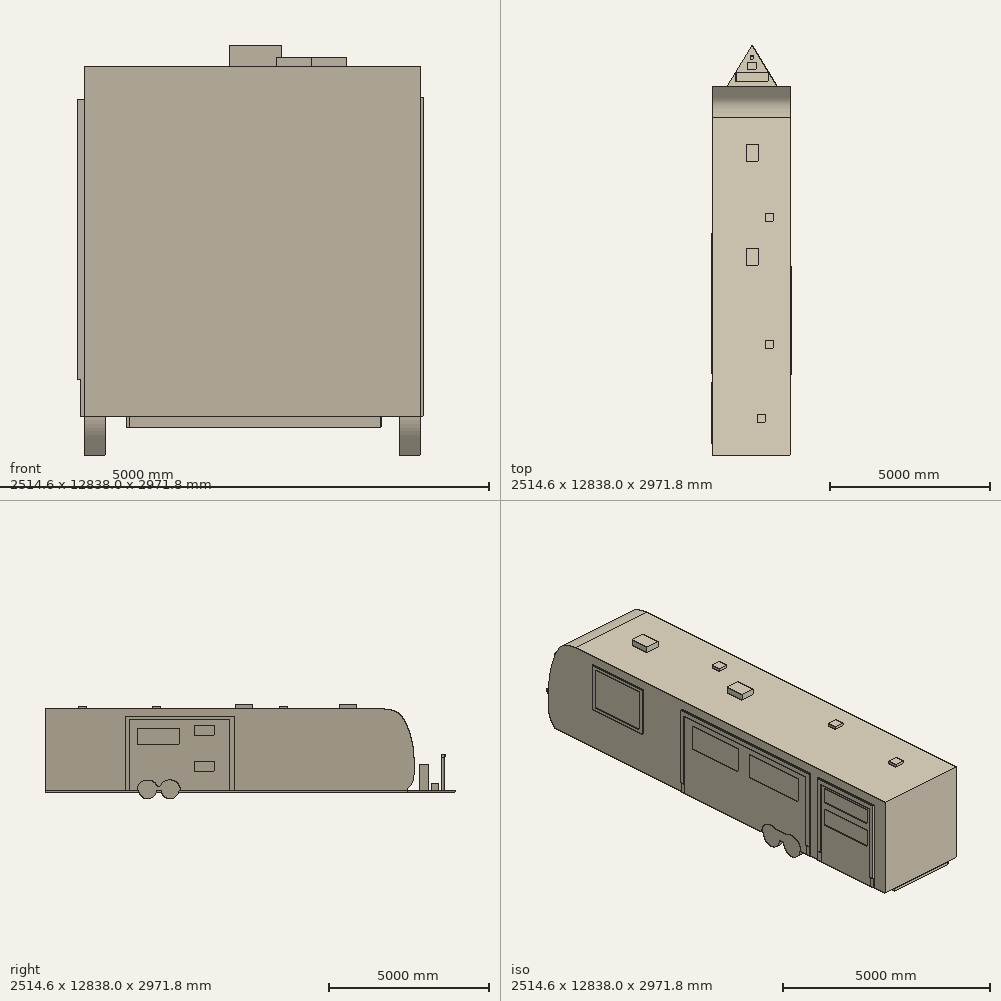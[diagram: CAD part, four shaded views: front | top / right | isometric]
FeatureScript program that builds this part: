
annotation { "Feature Type Name" : "Feature", "Feature Type Description" : "" }
export const myFeature = defineFeature(function(context is Context, id is Id, definition is map)
    precondition{}
    {
        {
            var Q0;
            Q0=qCreatedBy(makeId("Right.planeOp"),FACE);
            var sketch = newSketch(context, id + "F0", { "sketchPlane" : qUnion([Q0])});
            skLineSegment(sketch, "E0.bottom", {"start": v(-92.94, 2504.2) * mm, "end": v(11489.46, 2504.2) * mm});
            skLineSegment(sketch, "E0.top", {"start": v(-92.94, -35.8) * mm, "end": v(11489.46, -35.8) * mm});
            skLineSegment(sketch, "E0.left", {"start": v(-92.94, 2504.2) * mm, "end": v(-92.94, -35.8) * mm});
            skLineSegment(sketch, "E0.right", {"start": v(11489.46, 2504.2) * mm, "end": v(11489.46, -35.8) * mm});
            skSolve(sketch);
        }
        {
            var Q0;
            Q0 = qSketchRegion(id + "F0", true);
            extrude(context, id + "F1", {"entities" : qUnion([Q0]), "depth" : 2438.4 * mm});
        }
        {
            var Q0;
            Q0=makeQuery(id+"F1.opExtrude","CAP_FACE",FACE,{"disambiguationData":[OSD([sQuery(id+"F0.wireOp",EDGE,"E0.bottom"),sQuery(id+"F0.wireOp",EDGE,"E0.top"),sQuery(id+"F0.wireOp",EDGE,"E0.left"),sQuery(id+"F0.wireOp",EDGE,"E0.right")])],"isStart":false});
            var sketch = newSketch(context, id + "F2", { "sketchPlane" : qUnion([Q0])});
            skFitSpline(sketch, "E1", {"points": [v(11227.22, -35.8) * mm, v(11399.13, 196.48) * mm, v(11452.15, 611.33) * mm, v(11421.45, 1291.05) * mm, v(11256.96, 1907.06) * mm, v(10951.77, 2379.6) * mm, v(10498.91, 2504.2) * mm], "startDerivative": vector(1581.34, 1665.5) * mm, "endDerivative": vector(-3034.29, 317.5) * mm});
            skSolve(sketch);
        }
        {
            var Q0;
            Q0 = qSketchRegion(id + "F2", true);
            var Q1;
            {var subQ0=sQuery(id+"F2.wireOp",EDGE,"E1");Q1=makeQuery(id+"F2.imprint","IMPRINT",FACE,{"disambiguationData":[TD([[makeQuery(id+"F2.imprint","IMPRINT",EDGE,{"derivedFrom":subQ0}),-1.0]])]});}
            extrude(context, id + "F3", {"entities" : qUnion([Q0, Q1]), "operationType" : NewBodyOperationType.REMOVE, "endBound" : BoundingType.THROUGH_ALL, "oppositeDirection" : true, "depth" : 25.4 * mm});
        }
        {
            var Q0;
            Q0=makeQuery(id+"F1.opExtrude","CAP_FACE",FACE,{"disambiguationData":[OSD([sQuery(id+"F0.wireOp",EDGE,"E0.bottom"),sQuery(id+"F0.wireOp",EDGE,"E0.top"),sQuery(id+"F0.wireOp",EDGE,"E0.left"),sQuery(id+"F0.wireOp",EDGE,"E0.right")])],"isStart":true});
            var sketch = newSketch(context, id + "F4", { "sketchPlane" : qUnion([Q0])});
            skLineSegment(sketch, "E2", {"start": v(-11413.21, 234.93) * mm, "end": v(-3972.23, 234.93) * mm});
            skLineSegment(sketch, "E3.bottom", {"start": v(-294.2, 2264.02) * mm, "end": v(-2196.7, 2264.02) * mm});
            skLineSegment(sketch, "E3.top", {"start": v(-294.2, -35.8) * mm, "end": v(-2196.7, -35.8) * mm});
            skLineSegment(sketch, "E3.left", {"start": v(-294.2, 2264.02) * mm, "end": v(-294.2, -35.8) * mm});
            skLineSegment(sketch, "E3.right", {"start": v(-2196.7, 2264.02) * mm, "end": v(-2196.7, -35.8) * mm});
            skLineSegment(sketch, "E4.bottom", {"start": v(-2467, 2264.02) * mm, "end": v(-6864.6, 2264.02) * mm});
            skLineSegment(sketch, "E4.top", {"start": v(-2467, -35.8) * mm, "end": v(-6864.6, -35.8) * mm});
            skLineSegment(sketch, "E4.left", {"start": v(-2467, 2264.02) * mm, "end": v(-2467, -35.8) * mm});
            skLineSegment(sketch, "E4.right", {"start": v(-6864.6, 2264.02) * mm, "end": v(-6864.6, -35.8) * mm});
            skPoint(sketch, "E5.endSnap0", {"position": v(-4665.8, 2264.02) * mm});
            skLineSegment(sketch, "E6.bottom", {"start": v(-8189.46, 2264.02) * mm, "end": v(-9928.19, 2264.02) * mm});
            skLineSegment(sketch, "E6.top", {"start": v(-8189.46, 1028.62) * mm, "end": v(-9928.19, 1028.62) * mm});
            skLineSegment(sketch, "E6.left", {"start": v(-8189.46, 2264.02) * mm, "end": v(-8189.46, 1028.62) * mm});
            skLineSegment(sketch, "E6.right", {"start": v(-9928.19, 2264.02) * mm, "end": v(-9928.19, 1028.62) * mm});
            skLineSegment(sketch, "E7.bottom", {"start": v(-9823.16, 2172.22) * mm, "end": v(-8306.15, 2172.22) * mm});
            skLineSegment(sketch, "E7.top", {"start": v(-9823.16, 1121.98) * mm, "end": v(-8306.15, 1121.98) * mm});
            skLineSegment(sketch, "E7.left", {"start": v(-9823.16, 2172.22) * mm, "end": v(-9823.16, 1121.98) * mm});
            skLineSegment(sketch, "E7.right", {"start": v(-8306.15, 2172.22) * mm, "end": v(-8306.15, 1121.98) * mm});
            skLineSegment(sketch, "E8.bottom", {"start": v(-6765.8, 2148.88) * mm, "end": v(-5554.68, 2148.88) * mm});
            skLineSegment(sketch, "E8.left", {"start": v(-6765.8, 2148.88) * mm, "end": v(-6765.8, 234.93) * mm});
            skLineSegment(sketch, "E8.right", {"start": v(-2582.35, 2148.88) * mm, "end": v(-2582.35, 234.93) * mm});
            skLineSegment(sketch, "E9", {"start": v(-5554.68, 2148.88) * mm, "end": v(-2582.35, 2148.88) * mm});
            skLineSegment(sketch, "E10.bottom", {"start": v(-2075.31, 2148.88) * mm, "end": v(-405.84, 2148.88) * mm});
            skLineSegment(sketch, "E10.left", {"start": v(-2075.31, 2148.88) * mm, "end": v(-2075.31, 234.93) * mm});
            skLineSegment(sketch, "E10.right", {"start": v(-405.84, 2148.88) * mm, "end": v(-405.84, 234.93) * mm});
            skLineSegment(sketch, "E11.bottom", {"start": v(-6515.67, 1954) * mm, "end": v(-4923.13, 1954) * mm});
            skLineSegment(sketch, "E11.top", {"start": v(-6515.67, 1310.39) * mm, "end": v(-4923.13, 1310.39) * mm});
            skLineSegment(sketch, "E11.left", {"start": v(-6515.67, 1954) * mm, "end": v(-6515.67, 1310.39) * mm});
            skLineSegment(sketch, "E11.right", {"start": v(-4923.13, 1954) * mm, "end": v(-4923.13, 1310.39) * mm});
            skLineSegment(sketch, "E12.bottom", {"start": v(-4560.07, 1954) * mm, "end": v(-2860.27, 1954) * mm});
            skLineSegment(sketch, "E12.top", {"start": v(-4560.07, 1310.39) * mm, "end": v(-2860.27, 1310.39) * mm});
            skLineSegment(sketch, "E12.left", {"start": v(-4560.07, 1954) * mm, "end": v(-4560.07, 1310.39) * mm});
            skLineSegment(sketch, "E12.right", {"start": v(-2860.27, 1954) * mm, "end": v(-2860.27, 1310.39) * mm});
            skPoint(sketch, "E13.orphan", {"position": v(451.54, 2264.02) * mm});
            skLineSegment(sketch, "E14.bottom", {"start": v(-1987.57, 2047.8) * mm, "end": v(-505.56, 2047.8) * mm});
            skLineSegment(sketch, "E14.top", {"start": v(-1987.57, 1662.7) * mm, "end": v(-505.56, 1662.7) * mm});
            skLineSegment(sketch, "E14.left", {"start": v(-1987.57, 2047.8) * mm, "end": v(-1987.57, 1662.7) * mm});
            skLineSegment(sketch, "E14.right", {"start": v(-505.56, 2047.8) * mm, "end": v(-505.56, 1662.7) * mm});
            skLineSegment(sketch, "E15.bottom", {"start": v(-1975.9, 1487.66) * mm, "end": v(-517.23, 1487.66) * mm});
            skLineSegment(sketch, "E15.top", {"start": v(-1975.9, 1032.56) * mm, "end": v(-517.23, 1032.56) * mm});
            skLineSegment(sketch, "E15.left", {"start": v(-1975.9, 1487.66) * mm, "end": v(-1975.9, 1032.56) * mm});
            skLineSegment(sketch, "E15.right", {"start": v(-517.23, 1487.66) * mm, "end": v(-517.23, 1032.56) * mm});
            skCircle(sketch, "E16", {"center": v(-3107.83, -35.8) * mm, "radius": 279.4 * mm});
            skCircle(sketch, "E17", {"center": v(-3807.99, -35.8) * mm, "radius": 279.4 * mm});
            skArc(sketch, "E18", {"start": v(-3542.35, 130.2) * mm, "mid": v(-3897.19, 267.2) * mm, "end": v(-4127.14, -35.8) * mm});
            skArc(sketch, "E19", {"start": v(-2783.43, -35.8) * mm, "mid": v(-3019.85, 266.52) * mm, "end": v(-3378.61, 130.2) * mm});
            skArc(sketch, "E20", {"start": v(-3542.35, 130.2) * mm, "mid": v(-3460.48, 80.08) * mm, "end": v(-3378.61, 130.2) * mm});
            skLineSegment(sketch, "E21.trimOffspring", {"start": v(-3649.39, 234.93) * mm, "end": v(-3268.73, 234.93) * mm});
            skLineSegment(sketch, "E22.trimOffspring", {"start": v(-2944.75, 234.93) * mm, "end": v(92.94, 234.93) * mm});
            skLineSegment(sketch, "E23", {"start": v(-6765.8, 234.93) * mm, "end": v(-6765.8, -35.8) * mm});
            skLineSegment(sketch, "E24", {"start": v(-2582.35, 234.93) * mm, "end": v(-2582.35, -35.8) * mm});
            skLineSegment(sketch, "E25", {"start": v(-2075.31, 234.93) * mm, "end": v(-2075.31, -35.8) * mm});
            skLineSegment(sketch, "E26", {"start": v(-405.84, 234.93) * mm, "end": v(-405.84, -35.8) * mm});
            skSolve(sketch);
        }
        {
            var Q0;
            Q0=makeQuery(id+"F4.imprint","IMPRINT",FACE,{"disambiguationData":[TD([[makeQuery(id+"F4.imprint","IMPRINT",EDGE,{"derivedFrom":sQuery(id+"F4.wireOp",EDGE,"E6.top")}),-1.0]])]});
            var Q1;
            Q1=makeQuery(id+"F4.imprint","IMPRINT",FACE,{"disambiguationData":[TD([[makeQuery(id+"F4.imprint","IMPRINT",EDGE,{"derivedFrom":sQuery(id+"F4.wireOp",EDGE,"E8.bottom")}),1.0]])]});
            var Q2;
            {var subQ1=sQuery(id+"F4.wireOp",EDGE,"E3.bottom");Q2=makeQuery(id+"F4.imprint","IMPRINT",FACE,{"disambiguationData":[TD([[makeQuery(id+"F4.imprint","IMPRINT",EDGE,{"derivedFrom":subQ1}),1.0]])]});}
            extrude(context, id + "F5", {"entities" : qUnion([Q0, Q1, Q2]), "operationType" : NewBodyOperationType.ADD, "depth" : 25.4 * mm});
        }
        {
            var Q0;
            {var subQ0=sQuery(id+"F4.wireOp",EDGE,"E23");Q0=makeQuery(id+"F4.imprint","IMPRINT",FACE,{"disambiguationData":[TD([[makeQuery(id+"F4.imprint","IMPRINT",EDGE,{"derivedFrom":subQ0}),-1.0]])]});}
            var Q1;
            {var subQ3=sQuery(id+"F4.wireOp",EDGE,"E24");Q1=makeQuery(id+"F4.imprint","IMPRINT",FACE,{"disambiguationData":[TD([[makeQuery(id+"F4.imprint","IMPRINT",EDGE,{"derivedFrom":subQ3}),1.0]])]});}
            var Q2;
            {var subQ3=sQuery(id+"F4.wireOp",EDGE,"E25");Q2=makeQuery(id+"F4.imprint","IMPRINT",FACE,{"disambiguationData":[TD([[makeQuery(id+"F4.imprint","IMPRINT",EDGE,{"derivedFrom":subQ3}),-1.0]])]});}
            var Q3;
            {var subQ3=sQuery(id+"F4.wireOp",EDGE,"E26");Q3=makeQuery(id+"F4.imprint","IMPRINT",FACE,{"disambiguationData":[TD([[makeQuery(id+"F4.imprint","IMPRINT",EDGE,{"derivedFrom":subQ3}),1.0]])]});}
            var Q4;
            Q4=makeQuery(id+"F5.opExtrude","CAP_FACE",FACE,{"disambiguationData":[OSD([sQuery(id+"F4.wireOp",EDGE,"E2"),sQuery(id+"F4.wireOp",EDGE,"E4.left"),sQuery(id+"F4.wireOp",EDGE,"E4.right"),sQuery(id+"F4.wireOp",EDGE,"E8.bottom"),sQuery(id+"F4.wireOp",EDGE,"E8.left"),sQuery(id+"F4.wireOp",EDGE,"E8.right"),sQuery(id+"F4.wireOp",EDGE,"E9"),sQuery(id+"F4.wireOp",EDGE,"E4.bottom"),sQuery(id+"F4.wireOp",EDGE,"E22.trimOffspring")])],"isStart":false});
            var Q5;
            Q5=makeQuery(id+"F5.opExtrude","CAP_FACE",FACE,{"disambiguationData":[OSD([sQuery(id+"F4.wireOp",EDGE,"E3.left"),sQuery(id+"F4.wireOp",EDGE,"E3.right"),sQuery(id+"F4.wireOp",EDGE,"E3.bottom"),sQuery(id+"F4.wireOp",EDGE,"E10.left"),sQuery(id+"F4.wireOp",EDGE,"E10.right"),sQuery(id+"F4.wireOp",EDGE,"E10.bottom"),sQuery(id+"F4.wireOp",EDGE,"E22.trimOffspring")])],"isStart":false});
            extrude(context, id + "F6", {"entities" : qUnion([Q0, Q1, Q2, Q3, Q4, Q5]), "operationType" : NewBodyOperationType.ADD, "depth" : 25.4 * mm});
        }
        {
            var Q0;
            Q0=makeQuery(id+"F4.imprint","IMPRINT",FACE,{"disambiguationData":[TD([[makeQuery(id+"F4.imprint","IMPRINT",EDGE,{"derivedFrom":sQuery(id+"F4.wireOp",EDGE,"E8.bottom")}),-1.0]])]});
            var Q1;
            {var subQ3=sQuery(id+"F4.wireOp",EDGE,"E23");Q1=makeQuery(id+"F4.imprint","IMPRINT",FACE,{"disambiguationData":[TD([[makeQuery(id+"F4.imprint","IMPRINT",EDGE,{"derivedFrom":subQ3}),1.0]])]});}
            var Q2;
            {var subQ3=sQuery(id+"F4.wireOp",EDGE,"E24");Q2=makeQuery(id+"F4.imprint","IMPRINT",FACE,{"disambiguationData":[TD([[makeQuery(id+"F4.imprint","IMPRINT",EDGE,{"derivedFrom":subQ3}),-1.0]])]});}
            var Q3;
            {var subQ0=sQuery(id+"F4.wireOp",EDGE,"E25");Q3=makeQuery(id+"F4.imprint","IMPRINT",FACE,{"disambiguationData":[TD([[makeQuery(id+"F4.imprint","IMPRINT",EDGE,{"derivedFrom":subQ0}),1.0]])]});}
            var Q4;
            {var subQ1=sQuery(id+"F4.wireOp",EDGE,"E10.left");Q4=makeQuery(id+"F4.imprint","IMPRINT",FACE,{"disambiguationData":[TD([[makeQuery(id+"F4.imprint","IMPRINT",EDGE,{"derivedFrom":subQ1}),1.0]])]});}
            var Q5;
            Q5=makeQuery(id+"F4.imprint","IMPRINT",FACE,{"disambiguationData":[TD([[makeQuery(id+"F4.imprint","IMPRINT",EDGE,{"derivedFrom":sQuery(id+"F4.wireOp",EDGE,"E7.bottom")}),-1.0]])]});
            extrude(context, id + "F7", {"entities" : qUnion([Q0, Q1, Q2, Q3, Q4, Q5]), "operationType" : NewBodyOperationType.ADD, "depth" : 12.7 * mm});
        }
        {
            var Q0;
            Q0=makeQuery(id+"F7.opExtrude","CAP_EDGE",EDGE,{"disambiguationData":[OSD([sQuery(id+"F4.wireOp",EDGE,"E14.left")])],"isStart":false});
            var Q1;
            Q1=makeQuery(id+"F7.opExtrude","CAP_EDGE",EDGE,{"disambiguationData":[OSD([sQuery(id+"F4.wireOp",EDGE,"E14.bottom")])],"isStart":false});
            fillet(context, id + "F8", {"entities" : qUnion([Q0, Q1]), "radius" : 5.08 * mm, "tangentPropagation" : true, "allowEdgeOverflow" : false});
        }
        {
            var Q0;
            {var subQ0=sQuery(id+"F4.wireOp",EDGE,"E17");var subQ1=sQuery(id+"F4.wireOp",EDGE,"E4.top");var subQ2=makeQuery(id+"F4.imprint","INTERSECT",VERTEX,{"disambiguationData":[OD(0.0)],"derivedFrom":[subQ1,subQ0]});Q0=makeQuery(id+"F4.imprint","IMPRINT",FACE,{"disambiguationData":[TD([[makeQuery(id+"F4.imprint","IMPRINT",EDGE,{"disambiguationData":[TD([[subQ2,-1.0]])],"derivedFrom":subQ1}),-1.0]])]});}
            var Q1;
            {var subQ0=sQuery(id+"F4.wireOp",EDGE,"E17");var subQ1=sQuery(id+"F4.wireOp",EDGE,"E4.top");var subQ2=makeQuery(id+"F4.imprint","INTERSECT",VERTEX,{"disambiguationData":[OD(0.0)],"derivedFrom":[subQ1,subQ0]});Q1=makeQuery(id+"F4.imprint","IMPRINT",FACE,{"disambiguationData":[TD([[makeQuery(id+"F4.imprint","IMPRINT",EDGE,{"disambiguationData":[TD([[subQ2,-1.0]])],"derivedFrom":subQ1}),1.0]])]});}
            var Q2;
            {var subQ0=sQuery(id+"F4.wireOp",EDGE,"E16");var subQ1=sQuery(id+"F4.wireOp",EDGE,"E4.top");var subQ2=makeQuery(id+"F4.imprint","INTERSECT",VERTEX,{"disambiguationData":[OD(0.0)],"derivedFrom":[subQ1,subQ0]});Q2=makeQuery(id+"F4.imprint","IMPRINT",FACE,{"disambiguationData":[TD([[makeQuery(id+"F4.imprint","IMPRINT",EDGE,{"disambiguationData":[TD([[subQ2,-1.0]])],"derivedFrom":subQ1}),1.0]])]});}
            var Q3;
            {var subQ0=sQuery(id+"F4.wireOp",EDGE,"E16");var subQ1=sQuery(id+"F4.wireOp",EDGE,"E4.top");var subQ2=makeQuery(id+"F4.imprint","INTERSECT",VERTEX,{"disambiguationData":[OD(0.0)],"derivedFrom":[subQ1,subQ0]});Q3=makeQuery(id+"F4.imprint","IMPRINT",FACE,{"disambiguationData":[TD([[makeQuery(id+"F4.imprint","IMPRINT",EDGE,{"disambiguationData":[TD([[subQ2,-1.0]])],"derivedFrom":subQ1}),-1.0]])]});}
            extrude(context, id + "F9", {"entities" : qUnion([Q0, Q1, Q2, Q3]), "operationType" : NewBodyOperationType.ADD, "oppositeDirection" : true, "depth" : 152.4 * mm});
        }
        {
            var Q0;
            Q0=makeQuery(id+"F1.opExtrude","CAP_FACE",FACE,{"disambiguationData":[OSD([sQuery(id+"F0.wireOp",EDGE,"E0.bottom"),sQuery(id+"F0.wireOp",EDGE,"E0.top"),sQuery(id+"F0.wireOp",EDGE,"E0.left"),sQuery(id+"F0.wireOp",EDGE,"E0.right")])],"isStart":false});
            var sketch = newSketch(context, id + "F10", { "sketchPlane" : qUnion([Q0])});
            skCircle(sketch, "E27", {"center": v(3106.1, -35.8) * mm, "radius": 279.4 * mm});
            skCircle(sketch, "E28", {"center": v(3810.96, -35.8) * mm, "radius": 279.4 * mm});
            skArc(sketch, "E29", {"start": v(3378.7, 135.27) * mm, "mid": v(3015.5, 266.37) * mm, "end": v(2775.1, -35.8) * mm});
            skArc(sketch, "E30", {"start": v(4130.28, -35.8) * mm, "mid": v(3897.32, 267.74) * mm, "end": v(3538.36, 135.27) * mm});
            skArc(sketch, "E31", {"start": v(3378.7, 135.27) * mm, "mid": v(3398.12, 103.41) * mm, "end": v(3429.4, 83.07) * mm});
            skLineSegment(sketch, "E32", {"start": v(11412.26, 231.97) * mm, "end": v(3977.8, 231.97) * mm});
            skLineSegment(sketch, "E33.trimOffspring", {"start": v(2935.84, 231.97) * mm, "end": v(-92.94, 231.97) * mm});
            skLineSegment(sketch, "E34.trimOffspring", {"start": v(3637.72, 231.97) * mm, "end": v(3275.74, 231.97) * mm});
            skLineSegment(sketch, "E35.bottom", {"start": v(2402.79, -35.8) * mm, "end": v(5820.45, -35.8) * mm});
            skLineSegment(sketch, "E35.top", {"start": v(2402.79, 2278.16) * mm, "end": v(5820.45, 2278.16) * mm});
            skLineSegment(sketch, "E35.left", {"start": v(2402.79, -35.8) * mm, "end": v(2402.79, 2278.16) * mm});
            skLineSegment(sketch, "E35.right", {"start": v(5820.45, -35.8) * mm, "end": v(5820.45, 2278.16) * mm});
            skLineSegment(sketch, "E36.bottom", {"start": v(2541.72, 2157.75) * mm, "end": v(5663, 2157.75) * mm});
            skLineSegment(sketch, "E36.left", {"start": v(2541.72, 2157.75) * mm, "end": v(2541.72, 83.07) * mm});
            skLineSegment(sketch, "E36.right", {"start": v(5663, 2157.75) * mm, "end": v(5663, 83.07) * mm});
            skLineSegment(sketch, "E37.trimOffspring", {"start": v(3429.4, 83.07) * mm, "end": v(3487.66, 83.07) * mm});
            skArc(sketch, "E38.trimOffspring", {"start": v(3487.66, 83.07) * mm, "mid": v(3518.94, 103.41) * mm, "end": v(3538.36, 135.27) * mm});
            skLineSegment(sketch, "E39", {"start": v(5663.45, -35.8) * mm, "end": v(5663, 83.07) * mm});
            skLineSegment(sketch, "E40", {"start": v(2534.2, -35.8) * mm, "end": v(2541.72, 83.07) * mm});
            skLineSegment(sketch, "E41.bottom", {"start": v(2778.91, 1890.63) * mm, "end": v(4088.83, 1890.63) * mm});
            skLineSegment(sketch, "E41.top", {"start": v(2778.91, 1402) * mm, "end": v(4088.83, 1402) * mm});
            skLineSegment(sketch, "E41.left", {"start": v(2778.91, 1890.63) * mm, "end": v(2778.91, 1402) * mm});
            skLineSegment(sketch, "E41.right", {"start": v(4088.83, 1890.63) * mm, "end": v(4088.83, 1402) * mm});
            skSolve(sketch);
        }
        {
            var Q0;
            {var subQ5=sQuery(id+"F10.wireOp",EDGE,"E39");Q0=makeQuery(id+"F10.imprint","IMPRINT",FACE,{"disambiguationData":[TD([[makeQuery(id+"F10.imprint","IMPRINT",EDGE,{"derivedFrom":subQ5}),-1.0]])]});}
            var Q1;
            {var subQ0=sQuery(id+"F10.wireOp",EDGE,"E40");Q1=makeQuery(id+"F10.imprint","IMPRINT",FACE,{"disambiguationData":[TD([[makeQuery(id+"F10.imprint","IMPRINT",EDGE,{"derivedFrom":subQ0}),1.0]])]});}
            var Q2;
            {var subQ1=sQuery(id+"F10.wireOp",EDGE,"E35.top");Q2=makeQuery(id+"F10.imprint","IMPRINT",FACE,{"disambiguationData":[TD([[makeQuery(id+"F10.imprint","IMPRINT",EDGE,{"derivedFrom":subQ1}),-1.0]])]});}
            extrude(context, id + "F11", {"entities" : qUnion([Q0, Q1, Q2]), "operationType" : NewBodyOperationType.ADD, "depth" : 25.4 * mm});
        }
        {
            var Q0;
            {var subQ4=sQuery(id+"F10.wireOp",EDGE,"E34.trimOffspring");Q0=makeQuery(id+"F10.imprint","IMPRINT",FACE,{"disambiguationData":[TD([[makeQuery(id+"F10.imprint","IMPRINT",EDGE,{"derivedFrom":subQ4}),-1.0]])]});}
            var Q1;
            {var subQ0=sQuery(id+"F10.wireOp",EDGE,"E40");Q1=makeQuery(id+"F10.imprint","IMPRINT",FACE,{"disambiguationData":[TD([[makeQuery(id+"F10.imprint","IMPRINT",EDGE,{"derivedFrom":subQ0}),-1.0]])]});}
            var Q2;
            {var subQ1=sQuery(id+"F10.wireOp",EDGE,"E31");Q2=makeQuery(id+"F10.imprint","IMPRINT",FACE,{"disambiguationData":[TD([[makeQuery(id+"F10.imprint","IMPRINT",EDGE,{"derivedFrom":subQ1}),1.0]])]});}
            var Q3;
            {var subQ0=sQuery(id+"F10.wireOp",EDGE,"E39");Q3=makeQuery(id+"F10.imprint","IMPRINT",FACE,{"disambiguationData":[TD([[makeQuery(id+"F10.imprint","IMPRINT",EDGE,{"derivedFrom":subQ0}),1.0]])]});}
            extrude(context, id + "F12", {"entities" : qUnion([Q0, Q1, Q2, Q3]), "operationType" : NewBodyOperationType.ADD, "depth" : 12.7 * mm});
        }
        {
            var Q0;
            {var subQ0=sQuery(id+"F10.wireOp",EDGE,"E35.bottom");var subQ1=sQuery(id+"F10.wireOp",EDGE,"E27");var subQ2=makeQuery(id+"F10.imprint","INTERSECT",VERTEX,{"disambiguationData":[OD(0.0)],"derivedFrom":[subQ1,subQ0]});Q0=makeQuery(id+"F10.imprint","IMPRINT",FACE,{"disambiguationData":[TD([[makeQuery(id+"F10.imprint","IMPRINT",EDGE,{"disambiguationData":[TD([[subQ2,1.0]])],"derivedFrom":subQ1}),1.0]])]});}
            var Q1;
            {var subQ0=sQuery(id+"F10.wireOp",EDGE,"E35.bottom");var subQ1=sQuery(id+"F10.wireOp",EDGE,"E27");var subQ2=makeQuery(id+"F10.imprint","INTERSECT",VERTEX,{"disambiguationData":[OD(0.0)],"derivedFrom":[subQ1,subQ0]});Q1=makeQuery(id+"F10.imprint","IMPRINT",FACE,{"disambiguationData":[TD([[makeQuery(id+"F10.imprint","IMPRINT",EDGE,{"disambiguationData":[TD([[subQ2,-1.0]])],"derivedFrom":subQ1}),1.0]])]});}
            var Q2;
            {var subQ0=sQuery(id+"F10.wireOp",EDGE,"E35.bottom");var subQ1=sQuery(id+"F10.wireOp",EDGE,"E28");var subQ2=makeQuery(id+"F10.imprint","INTERSECT",VERTEX,{"disambiguationData":[OD(0.0)],"derivedFrom":[subQ1,subQ0]});Q2=makeQuery(id+"F10.imprint","IMPRINT",FACE,{"disambiguationData":[TD([[makeQuery(id+"F10.imprint","IMPRINT",EDGE,{"disambiguationData":[TD([[subQ2,-1.0]])],"derivedFrom":subQ1}),1.0]])]});}
            var Q3;
            {var subQ0=sQuery(id+"F10.wireOp",EDGE,"E35.bottom");var subQ1=sQuery(id+"F10.wireOp",EDGE,"E28");var subQ2=makeQuery(id+"F10.imprint","INTERSECT",VERTEX,{"disambiguationData":[OD(0.0)],"derivedFrom":[subQ1,subQ0]});Q3=makeQuery(id+"F10.imprint","IMPRINT",FACE,{"disambiguationData":[TD([[makeQuery(id+"F10.imprint","IMPRINT",EDGE,{"disambiguationData":[TD([[subQ2,1.0]])],"derivedFrom":subQ1}),1.0]])]});}
            extrude(context, id + "F13", {"entities" : qUnion([Q0, Q1, Q2, Q3]), "operationType" : NewBodyOperationType.ADD, "oppositeDirection" : true, "depth" : 152.4 * mm});
        }
        {
            var Q0;
            {var subQ0=sQuery(id+"F10.wireOp",EDGE,"E35.bottom");var subQ1=makeQuery(id+"F10.imprint","INTERSECT",VERTEX,{"derivedFrom":[subQ0,sQuery(id+"F10.wireOp",EDGE,"E39")]});var subQ2=makeQuery(id+"F10.imprint","INTERSECT",VERTEX,{"derivedFrom":[subQ0,sQuery(id+"F10.wireOp",EDGE,"E40")]});var subQ3=sQuery(id+"F0.wireOp",EDGE,"E0.top");var subQ5=sQuery(id+"F4.wireOp",EDGE,"E4.top");var subQ6=makeQuery(id+"F4.imprint","INTERSECT",VERTEX,{"derivedFrom":[subQ5,sQuery(id+"F4.wireOp",EDGE,"E23")]});var subQ7=makeQuery(id+"F4.imprint","INTERSECT",VERTEX,{"derivedFrom":[subQ5,sQuery(id+"F4.wireOp",EDGE,"E24")]});var subQ8=sQuery(id+"F4.wireOp",EDGE,"E3.top");Q0=makeQuery(id+"F12.boolean.opBoolean","MERGE",FACE,{"derivedFrom":[makeQuery(id+"F11.boolean.opBoolean","MERGE",FACE,{"derivedFrom":[makeQuery(id+"F7.boolean.opBoolean","MERGE",FACE,{"derivedFrom":[makeQuery(id+"F6.boolean.opBoolean","MERGE",FACE,{"derivedFrom":[makeQuery(id+"F1.opExtrude","SWEPT_FACE",FACE,{"disambiguationData":[OSD([subQ3])]}),makeQuery(id+"F6.opExtrude","SWEPT_FACE",FACE,{"disambiguationData":[OSD([subQ8]),TDD([makeQuery(id+"F4.imprint","IMPRINT",EDGE,{"disambiguationData":[TD([[makeQuery(id+"F4.imprint","INTERSECT",VERTEX,{"derivedFrom":[subQ8,sQuery(id+"F4.wireOp",EDGE,"E26")]}),1.0]])],"derivedFrom":subQ8})])]}),makeQuery(id+"F6.opExtrude","SWEPT_FACE",FACE,{"disambiguationData":[OSD([subQ8]),TDD([makeQuery(id+"F4.imprint","IMPRINT",EDGE,{"disambiguationData":[TD([[makeQuery(id+"F4.imprint","INTERSECT",VERTEX,{"derivedFrom":[subQ8,sQuery(id+"F4.wireOp",EDGE,"E25")]}),-1.0]])],"derivedFrom":subQ8})])]}),makeQuery(id+"F6.opExtrude","SWEPT_FACE",FACE,{"disambiguationData":[OSD([subQ5]),TDD([makeQuery(id+"F4.imprint","IMPRINT",EDGE,{"disambiguationData":[TD([[subQ7,1.0]])],"derivedFrom":subQ5})])]}),makeQuery(id+"F6.opExtrude","SWEPT_FACE",FACE,{"disambiguationData":[OSD([subQ5]),TDD([makeQuery(id+"F4.imprint","IMPRINT",EDGE,{"disambiguationData":[TD([[subQ6,-1.0]])],"derivedFrom":subQ5})])]})]}),makeQuery(id+"F7.opExtrude","SWEPT_FACE",FACE,{"disambiguationData":[OSD([subQ8])]}),makeQuery(id+"F7.opExtrude","SWEPT_FACE",FACE,{"disambiguationData":[OSD([subQ5]),TDD([makeQuery(id+"F4.imprint","IMPRINT",EDGE,{"disambiguationData":[TD([[makeQuery(id+"F4.imprint","INTERSECT",VERTEX,{"derivedFrom":[subQ5,sQuery(id+"F4.wireOp",EDGE,"E19")]}),1.0]])],"derivedFrom":subQ5})])]}),makeQuery(id+"F7.opExtrude","SWEPT_FACE",FACE,{"disambiguationData":[OSD([subQ5]),TDD([makeQuery(id+"F4.imprint","IMPRINT",EDGE,{"disambiguationData":[TD([[makeQuery(id+"F4.imprint","INTERSECT",VERTEX,{"derivedFrom":[subQ5,sQuery(id+"F4.wireOp",EDGE,"E18")]}),-1.0]])],"derivedFrom":subQ5})])]})]}),makeQuery(id+"F11.opExtrude","SWEPT_FACE",FACE,{"disambiguationData":[OSD([subQ0]),TDD([makeQuery(id+"F10.imprint","IMPRINT",EDGE,{"disambiguationData":[TD([[subQ2,1.0]])],"derivedFrom":subQ0})])]}),makeQuery(id+"F11.opExtrude","SWEPT_FACE",FACE,{"disambiguationData":[OSD([subQ0]),TDD([makeQuery(id+"F10.imprint","IMPRINT",EDGE,{"disambiguationData":[TD([[subQ1,-1.0]])],"derivedFrom":subQ0})])]})]}),makeQuery(id+"F12.opExtrude","SWEPT_FACE",FACE,{"disambiguationData":[OSD([subQ0]),TDD([makeQuery(id+"F10.imprint","IMPRINT",EDGE,{"disambiguationData":[TD([[makeQuery(id+"F10.imprint","INTERSECT",VERTEX,{"derivedFrom":[sQuery(id+"F10.wireOp",EDGE,"E29"),subQ0]}),1.0]])],"derivedFrom":subQ0})])]}),makeQuery(id+"F12.opExtrude","SWEPT_FACE",FACE,{"disambiguationData":[OSD([subQ0]),TDD([makeQuery(id+"F10.imprint","IMPRINT",EDGE,{"disambiguationData":[TD([[makeQuery(id+"F10.imprint","INTERSECT",VERTEX,{"derivedFrom":[sQuery(id+"F10.wireOp",EDGE,"E30"),subQ0]}),-1.0]])],"derivedFrom":subQ0})])]})]});}
            var sketch = newSketch(context, id + "F14", { "sketchPlane" : qUnion([Q0])});
            skLineSegment(sketch, "E42", {"start": v(304.51, -11227.22) * mm, "end": v(1230.43, -12745.1) * mm});
            skLineSegment(sketch, "E43", {"start": v(1230.43, -12745.1) * mm, "end": v(2156.35, -11227.22) * mm});
            skLineSegment(sketch, "E44", {"start": v(1219.2, -11227.22) * mm, "end": v(1230.43, -12318.8) * mm});
            skSolve(sketch);
        }
        {
            var Q0;
            {var subQ0=sQuery(id+"F14.wireOp",EDGE,"E42");Q0=makeQuery(id+"F14.imprint","IMPRINT",FACE,{"disambiguationData":[TD([[makeQuery(id+"F14.imprint","IMPRINT",EDGE,{"derivedFrom":subQ0}),1.0]])]});}
            var sketch = newSketch(context, id + "F15", { "sketchPlane" : qUnion([Q0])});
            skLineSegment(sketch, "E45", {"start": v(428.6, -11222.62) * mm, "end": v(1220.28, -12562.4) * mm});
            skLineSegment(sketch, "E46", {"start": v(1220.28, -12562.4) * mm, "end": v(2032.27, -11242.92) * mm});
            skSolve(sketch);
        }
        {
            var Q0;
            Q0=makeQuery(id+"F12.opExtrude","CAP_FACE",FACE,{"disambiguationData":[OSD([sQuery(id+"F10.wireOp",EDGE,"E29"),sQuery(id+"F10.wireOp",EDGE,"E30"),sQuery(id+"F10.wireOp",EDGE,"E31"),sQuery(id+"F10.wireOp",EDGE,"E35.bottom"),sQuery(id+"F10.wireOp",EDGE,"E36.bottom"),sQuery(id+"F10.wireOp",EDGE,"E36.left"),sQuery(id+"F10.wireOp",EDGE,"E36.right"),sQuery(id+"F10.wireOp",EDGE,"E37.trimOffspring"),sQuery(id+"F10.wireOp",EDGE,"E38.trimOffspring"),sQuery(id+"F10.wireOp",EDGE,"E39"),sQuery(id+"F10.wireOp",EDGE,"E40"),sQuery(id+"F10.wireOp",EDGE,"E41.bottom"),sQuery(id+"F10.wireOp",EDGE,"E41.top"),sQuery(id+"F10.wireOp",EDGE,"E41.left"),sQuery(id+"F10.wireOp",EDGE,"E41.right")])],"isStart":false});
            var sketch = newSketch(context, id + "F16", { "sketchPlane" : qUnion([Q0])});
            skLineSegment(sketch, "E47.bottom", {"start": v(4577.15, 1969.5) * mm, "end": v(5186.75, 1969.5) * mm});
            skLineSegment(sketch, "E47.top", {"start": v(4577.15, 1664.7) * mm, "end": v(5186.75, 1664.7) * mm});
            skLineSegment(sketch, "E47.left", {"start": v(4577.15, 1969.5) * mm, "end": v(4577.15, 1664.7) * mm});
            skLineSegment(sketch, "E47.right", {"start": v(5186.75, 1969.5) * mm, "end": v(5186.75, 1664.7) * mm});
            skLineSegment(sketch, "E48.bottom", {"start": v(4577.15, 858.86) * mm, "end": v(5186.75, 858.86) * mm});
            skLineSegment(sketch, "E48.top", {"start": v(4577.15, 554.06) * mm, "end": v(5186.75, 554.06) * mm});
            skLineSegment(sketch, "E48.left", {"start": v(4577.15, 858.86) * mm, "end": v(4577.15, 554.06) * mm});
            skLineSegment(sketch, "E48.right", {"start": v(5186.75, 858.86) * mm, "end": v(5186.75, 554.06) * mm});
            skSolve(sketch);
        }
        {
            var Q0;
            Q0=makeQuery(id+"F16.imprint","IMPRINT",FACE,{"disambiguationData":[TD([[makeQuery(id+"F16.imprint","IMPRINT",EDGE,{"derivedFrom":sQuery(id+"F16.wireOp",EDGE,"E47.bottom")}),-1.0]])]});
            var Q1;
            Q1=makeQuery(id+"F16.imprint","IMPRINT",FACE,{"disambiguationData":[TD([[makeQuery(id+"F16.imprint","IMPRINT",EDGE,{"derivedFrom":sQuery(id+"F16.wireOp",EDGE,"E48.bottom")}),-1.0]])]});
            extrude(context, id + "F17", {"entities" : qUnion([Q0, Q1]), "operationType" : NewBodyOperationType.ADD, "depth" : 6.35 * mm});
        }
        {
            var Q0;
            Q0=makeQuery(id+"F1.opExtrude","SWEPT_FACE",FACE,{"disambiguationData":[OSD([sQuery(id+"F0.wireOp",EDGE,"E0.bottom")])]});
            var sketch = newSketch(context, id + "F18", { "sketchPlane" : qUnion([Q0])});
            skLineSegment(sketch, "E49", {"start": v(1218.85, 11455.41) * mm, "end": v(1218.85, 8266.61) * mm, "construction": true});
            skLineSegment(sketch, "E50.bottom", {"start": v(1053.2, 9636) * mm, "end": v(1434.2, 9636) * mm});
            skLineSegment(sketch, "E50.top", {"start": v(1053.2, 9128) * mm, "end": v(1434.2, 9128) * mm});
            skLineSegment(sketch, "E50.left", {"start": v(1053.2, 9636) * mm, "end": v(1053.2, 9128) * mm});
            skLineSegment(sketch, "E50.right", {"start": v(1434.2, 9636) * mm, "end": v(1434.2, 9128) * mm});
            skSolve(sketch);
        }
        {
            var Q0;
            Q0 = qSketchRegion(id + "F18", true);
            extrude(context, id + "F19", {"entities" : qUnion([Q0]), "operationType" : NewBodyOperationType.ADD, "depth" : 152.4 * mm});
        }
        {
            var Q0;
            Q0=makeQuery(id+"F1.opExtrude","SWEPT_FACE",FACE,{"disambiguationData":[OSD([sQuery(id+"F0.wireOp",EDGE,"E0.bottom")])]});
            var sketch = newSketch(context, id + "F20", { "sketchPlane" : qUnion([Q0])});
            skLineSegment(sketch, "E51", {"start": v(1053.2, 6373.33) * mm, "end": v(1053.2, 5865.33) * mm});
            skLineSegment(sketch, "E52.bottom", {"start": v(1053.2, 6373.33) * mm, "end": v(1434.2, 6373.33) * mm});
            skLineSegment(sketch, "E52.top", {"start": v(1053.2, 5865.33) * mm, "end": v(1434.2, 5865.33) * mm});
            skLineSegment(sketch, "E52.right", {"start": v(1434.2, 6373.33) * mm, "end": v(1434.2, 5865.33) * mm});
            skSolve(sketch);
        }
        {
            var Q0;
            Q0 = qSketchRegion(id + "F20", true);
            extrude(context, id + "F21", {"entities" : qUnion([Q0]), "operationType" : NewBodyOperationType.ADD, "depth" : 152.4 * mm});
        }
        {
            var Q0;
            Q0=makeQuery(id+"F1.opExtrude","SWEPT_FACE",FACE,{"disambiguationData":[OSD([sQuery(id+"F0.wireOp",EDGE,"E0.bottom")])]});
            var sketch = newSketch(context, id + "F22", { "sketchPlane" : qUnion([Q0])});
            skLineSegment(sketch, "E53.bottom", {"start": v(1651.16, 7493.1) * mm, "end": v(1905.16, 7493.1) * mm});
            skLineSegment(sketch, "E53.top", {"start": v(1651.16, 7239.1) * mm, "end": v(1905.16, 7239.1) * mm});
            skLineSegment(sketch, "E53.left", {"start": v(1651.16, 7493.1) * mm, "end": v(1651.16, 7239.1) * mm});
            skLineSegment(sketch, "E53.right", {"start": v(1905.16, 7493.1) * mm, "end": v(1905.16, 7239.1) * mm});
            skLineSegment(sketch, "E54.bottom", {"start": v(1905.16, 3515.57) * mm, "end": v(1651.16, 3515.57) * mm});
            skLineSegment(sketch, "E54.top", {"start": v(1905.16, 3261.57) * mm, "end": v(1651.16, 3261.57) * mm});
            skLineSegment(sketch, "E54.left", {"start": v(1905.16, 3515.57) * mm, "end": v(1905.16, 3261.57) * mm});
            skLineSegment(sketch, "E54.right", {"start": v(1651.16, 3515.57) * mm, "end": v(1651.16, 3261.57) * mm});
            skLineSegment(sketch, "E55.bottom", {"start": v(1397.16, 932.38) * mm, "end": v(1651.16, 932.38) * mm});
            skLineSegment(sketch, "E55.top", {"start": v(1397.16, 1186.38) * mm, "end": v(1651.16, 1186.38) * mm});
            skLineSegment(sketch, "E55.left", {"start": v(1397.16, 932.38) * mm, "end": v(1397.16, 1186.38) * mm});
            skLineSegment(sketch, "E55.right", {"start": v(1651.16, 932.38) * mm, "end": v(1651.16, 1186.38) * mm});
            skSolve(sketch);
        }
        {
            var Q0;
            Q0 = qSketchRegion(id + "F22", true);
            extrude(context, id + "F23", {"entities" : qUnion([Q0]), "operationType" : NewBodyOperationType.ADD, "depth" : 63.5 * mm});
        }
        {
            var Q0;
            {var subQ0=sQuery(id+"F14.wireOp",EDGE,"E42");Q0=makeQuery(id+"F14.imprint","IMPRINT",FACE,{"disambiguationData":[TD([[makeQuery(id+"F14.imprint","IMPRINT",EDGE,{"derivedFrom":subQ0}),1.0]])]});}
            extrude(context, id + "F24", {"entities" : qUnion([Q0]), "depth" : 76.2 * mm});
        }
        {
            var Q0;
            {var subQ0=sQuery(id+"F10.wireOp",EDGE,"E35.bottom");var subQ1=makeQuery(id+"F10.imprint","INTERSECT",VERTEX,{"derivedFrom":[subQ0,sQuery(id+"F10.wireOp",EDGE,"E39")]});var subQ2=makeQuery(id+"F10.imprint","INTERSECT",VERTEX,{"derivedFrom":[subQ0,sQuery(id+"F10.wireOp",EDGE,"E40")]});var subQ3=sQuery(id+"F0.wireOp",EDGE,"E0.top");var subQ5=sQuery(id+"F4.wireOp",EDGE,"E4.top");var subQ6=makeQuery(id+"F4.imprint","INTERSECT",VERTEX,{"derivedFrom":[subQ5,sQuery(id+"F4.wireOp",EDGE,"E23")]});var subQ7=makeQuery(id+"F4.imprint","INTERSECT",VERTEX,{"derivedFrom":[subQ5,sQuery(id+"F4.wireOp",EDGE,"E24")]});var subQ8=sQuery(id+"F4.wireOp",EDGE,"E3.top");Q0=makeQuery(id+"F12.boolean.opBoolean","MERGE",FACE,{"derivedFrom":[makeQuery(id+"F11.boolean.opBoolean","MERGE",FACE,{"derivedFrom":[makeQuery(id+"F7.boolean.opBoolean","MERGE",FACE,{"derivedFrom":[makeQuery(id+"F6.boolean.opBoolean","MERGE",FACE,{"derivedFrom":[makeQuery(id+"F1.opExtrude","SWEPT_FACE",FACE,{"disambiguationData":[OSD([subQ3])]}),makeQuery(id+"F6.opExtrude","SWEPT_FACE",FACE,{"disambiguationData":[OSD([subQ8]),TDD([makeQuery(id+"F4.imprint","IMPRINT",EDGE,{"disambiguationData":[TD([[makeQuery(id+"F4.imprint","INTERSECT",VERTEX,{"derivedFrom":[subQ8,sQuery(id+"F4.wireOp",EDGE,"E26")]}),1.0]])],"derivedFrom":subQ8})])]}),makeQuery(id+"F6.opExtrude","SWEPT_FACE",FACE,{"disambiguationData":[OSD([subQ8]),TDD([makeQuery(id+"F4.imprint","IMPRINT",EDGE,{"disambiguationData":[TD([[makeQuery(id+"F4.imprint","INTERSECT",VERTEX,{"derivedFrom":[subQ8,sQuery(id+"F4.wireOp",EDGE,"E25")]}),-1.0]])],"derivedFrom":subQ8})])]}),makeQuery(id+"F6.opExtrude","SWEPT_FACE",FACE,{"disambiguationData":[OSD([subQ5]),TDD([makeQuery(id+"F4.imprint","IMPRINT",EDGE,{"disambiguationData":[TD([[subQ7,1.0]])],"derivedFrom":subQ5})])]}),makeQuery(id+"F6.opExtrude","SWEPT_FACE",FACE,{"disambiguationData":[OSD([subQ5]),TDD([makeQuery(id+"F4.imprint","IMPRINT",EDGE,{"disambiguationData":[TD([[subQ6,-1.0]])],"derivedFrom":subQ5})])]})]}),makeQuery(id+"F7.opExtrude","SWEPT_FACE",FACE,{"disambiguationData":[OSD([subQ8])]}),makeQuery(id+"F7.opExtrude","SWEPT_FACE",FACE,{"disambiguationData":[OSD([subQ5]),TDD([makeQuery(id+"F4.imprint","IMPRINT",EDGE,{"disambiguationData":[TD([[makeQuery(id+"F4.imprint","INTERSECT",VERTEX,{"derivedFrom":[subQ5,sQuery(id+"F4.wireOp",EDGE,"E19")]}),1.0]])],"derivedFrom":subQ5})])]}),makeQuery(id+"F7.opExtrude","SWEPT_FACE",FACE,{"disambiguationData":[OSD([subQ5]),TDD([makeQuery(id+"F4.imprint","IMPRINT",EDGE,{"disambiguationData":[TD([[makeQuery(id+"F4.imprint","INTERSECT",VERTEX,{"derivedFrom":[subQ5,sQuery(id+"F4.wireOp",EDGE,"E18")]}),-1.0]])],"derivedFrom":subQ5})])]})]}),makeQuery(id+"F11.opExtrude","SWEPT_FACE",FACE,{"disambiguationData":[OSD([subQ0]),TDD([makeQuery(id+"F10.imprint","IMPRINT",EDGE,{"disambiguationData":[TD([[subQ2,1.0]])],"derivedFrom":subQ0})])]}),makeQuery(id+"F11.opExtrude","SWEPT_FACE",FACE,{"disambiguationData":[OSD([subQ0]),TDD([makeQuery(id+"F10.imprint","IMPRINT",EDGE,{"disambiguationData":[TD([[subQ1,-1.0]])],"derivedFrom":subQ0})])]})]}),makeQuery(id+"F12.opExtrude","SWEPT_FACE",FACE,{"disambiguationData":[OSD([subQ0]),TDD([makeQuery(id+"F10.imprint","IMPRINT",EDGE,{"disambiguationData":[TD([[makeQuery(id+"F10.imprint","INTERSECT",VERTEX,{"derivedFrom":[sQuery(id+"F10.wireOp",EDGE,"E29"),subQ0]}),1.0]])],"derivedFrom":subQ0})])]}),makeQuery(id+"F12.opExtrude","SWEPT_FACE",FACE,{"disambiguationData":[OSD([subQ0]),TDD([makeQuery(id+"F10.imprint","IMPRINT",EDGE,{"disambiguationData":[TD([[makeQuery(id+"F10.imprint","INTERSECT",VERTEX,{"derivedFrom":[sQuery(id+"F10.wireOp",EDGE,"E30"),subQ0]}),-1.0]])],"derivedFrom":subQ0})])]})]});}
            var sketch = newSketch(context, id + "F25", { "sketchPlane" : qUnion([Q0])});
            skLineSegment(sketch, "E56.bottom", {"start": v(2147.14, -11227.22) * mm, "end": v(331.65, -11227.22) * mm});
            skLineSegment(sketch, "E56.top", {"start": v(2147.14, 92.94) * mm, "end": v(331.65, 92.94) * mm});
            skLineSegment(sketch, "E56.left", {"start": v(2147.14, -11227.22) * mm, "end": v(2147.14, 92.94) * mm});
            skLineSegment(sketch, "E56.right", {"start": v(331.65, -11227.22) * mm, "end": v(331.65, 92.94) * mm});
            skSolve(sketch);
        }
        {
            var Q0;
            Q0 = qSketchRegion(id + "F25", true);
            extrude(context, id + "F26", {"entities" : qUnion([Q0]), "depth" : 76.2 * mm});
        }
        {
            var Q0;
            {var subQ0=sQuery(id+"F14.wireOp",EDGE,"E42");Q0=makeQuery(id+"F15.imprint","IMPRINT",FACE,{"disambiguationData":[TD([[makeQuery(id+"F15.imprint","IMPRINT",EDGE,{"derivedFrom":makeQuery(id+"F14.imprint","IMPRINT",EDGE,{"derivedFrom":subQ0})}),1.0]])]});}
            var sketch = newSketch(context, id + "F27", { "sketchPlane" : qUnion([Q0])});
            skLineSegment(sketch, "E57.bottom", {"start": v(717.77, -11909.02) * mm, "end": v(1733.59, -11909.02) * mm});
            skLineSegment(sketch, "E57.top", {"start": v(717.77, -11621.2) * mm, "end": v(1733.59, -11621.2) * mm});
            skLineSegment(sketch, "E57.left", {"start": v(717.77, -11909.02) * mm, "end": v(717.77, -11621.2) * mm});
            skLineSegment(sketch, "E57.right", {"start": v(1733.59, -11909.02) * mm, "end": v(1733.59, -11621.2) * mm});
            skSolve(sketch);
        }
        {
            var Q0;
            Q0 = qSketchRegion(id + "F27", true);
            extrude(context, id + "F28", {"entities" : qUnion([Q0]), "operationType" : NewBodyOperationType.ADD, "oppositeDirection" : true, "depth" : 812.8 * mm});
        }
        {
            var Q0;
            {var subQ0=sQuery(id+"F14.wireOp",EDGE,"E42");Q0=makeQuery(id+"F15.imprint","IMPRINT",FACE,{"disambiguationData":[TD([[makeQuery(id+"F15.imprint","IMPRINT",EDGE,{"derivedFrom":makeQuery(id+"F14.imprint","IMPRINT",EDGE,{"derivedFrom":subQ0})}),1.0]])]});}
            var sketch = newSketch(context, id + "F29", { "sketchPlane" : qUnion([Q0])});
            skCircle(sketch, "E58", {"center": v(1222.69, -12362.52) * mm, "radius": 48.24 * mm});
            skPoint(sketch, "E59.orphan", {"position": v(1107.7, -12363.44) * mm});
            skPoint(sketch, "E60.end.orphan", {"position": v(1337.67, -12361.6) * mm});
            skLineSegment(sketch, "E61.bottom", {"start": v(1071.06, -12223.65) * mm, "end": v(1362.2, -12223.65) * mm});
            skLineSegment(sketch, "E61.top", {"start": v(1071.06, -11995.2) * mm, "end": v(1362.2, -11995.2) * mm});
            skLineSegment(sketch, "E61.left", {"start": v(1071.06, -12223.65) * mm, "end": v(1071.06, -11995.2) * mm});
            skLineSegment(sketch, "E61.right", {"start": v(1362.2, -12223.65) * mm, "end": v(1362.2, -11995.2) * mm});
            skSolve(sketch);
        }
        {
            var Q0;
            Q0 = qSketchRegion(id + "F29", true);
            extrude(context, id + "F30", {"entities" : qUnion([Q0]), "operationType" : NewBodyOperationType.REMOVE, "endBound" : BoundingType.THROUGH_ALL, "oppositeDirection" : true, "depth" : 25.4 * mm});
        }
        {
            var Q0;
            Q0=makeQuery(id+"F29.imprint","IMPRINT",FACE,{"disambiguationData":[TD([[makeQuery(id+"F29.imprint","IMPRINT",EDGE,{"derivedFrom":sQuery(id+"F29.wireOp",EDGE,"E58")}),1.0]])]});
            extrude(context, id + "F31", {"entities" : qUnion([Q0]), "operationType" : NewBodyOperationType.ADD, "oppositeDirection" : true, "depth" : 1016 * mm});
        }
        {
            var Q0;
            Q0 = qSketchRegion(id + "F29", true);
            extrude(context, id + "F32", {"entities" : qUnion([Q0]), "operationType" : NewBodyOperationType.ADD, "oppositeDirection" : true, "depth" : 203.2 * mm});
        }
        {
            var Q0;
            Q0=makeQuery(id+"F31.opExtrude","CAP_FACE",FACE,{"disambiguationData":[OSD([sQuery(id+"F29.wireOp",EDGE,"E58")])],"isStart":false});
            var sketch = newSketch(context, id + "F33", { "sketchPlane" : qUnion([Q0])});
            skLineSegment(sketch, "E62.bottom", {"start": v(1166.29, 12416.8) * mm, "end": v(1276.03, 12416.8) * mm});
            skLineSegment(sketch, "E62.top", {"start": v(1166.29, 12311.04) * mm, "end": v(1276.03, 12311.04) * mm});
            skLineSegment(sketch, "E62.left", {"start": v(1166.29, 12416.8) * mm, "end": v(1166.29, 12311.04) * mm});
            skLineSegment(sketch, "E62.right", {"start": v(1276.03, 12416.8) * mm, "end": v(1276.03, 12311.04) * mm});
            skSolve(sketch);
        }
        {
            var Q0;
            Q0 = qSketchRegion(id + "F33", true);
            extrude(context, id + "F34", {"entities" : qUnion([Q0]), "operationType" : NewBodyOperationType.ADD, "depth" : 101.6 * mm});
        }
        {
            var Q0;
            Q0=makeQuery(id+"F34.opExtrude","SWEPT_EDGE",EDGE,{"disambiguationData":[OSD([sQuery(id+"F33.wireOp",EDGE,"E62.bottom"),sQuery(id+"F33.wireOp",EDGE,"E62.right")])]});
            var Q1;
            Q1=makeQuery(id+"F34.opExtrude","SWEPT_EDGE",EDGE,{"disambiguationData":[OSD([sQuery(id+"F33.wireOp",EDGE,"E62.top"),sQuery(id+"F33.wireOp",EDGE,"E62.right")])]});
            var Q2;
            Q2=makeQuery(id+"F34.opExtrude","CAP_EDGE",EDGE,{"disambiguationData":[OSD([sQuery(id+"F33.wireOp",EDGE,"E62.right")])],"isStart":false});
            var Q3;
            Q3=makeQuery(id+"F34.opExtrude","CAP_EDGE",EDGE,{"disambiguationData":[OSD([sQuery(id+"F33.wireOp",EDGE,"E62.bottom")])],"isStart":false});
            var Q4;
            Q4=makeQuery(id+"F34.opExtrude","CAP_EDGE",EDGE,{"disambiguationData":[OSD([sQuery(id+"F33.wireOp",EDGE,"E62.left")])],"isStart":false});
            var Q5;
            Q5=makeQuery(id+"F34.opExtrude","CAP_EDGE",EDGE,{"disambiguationData":[OSD([sQuery(id+"F33.wireOp",EDGE,"E62.top")])],"isStart":false});
            var Q6;
            Q6=makeQuery(id+"F34.opExtrude","SWEPT_EDGE",EDGE,{"disambiguationData":[OSD([sQuery(id+"F33.wireOp",EDGE,"E62.top"),sQuery(id+"F33.wireOp",EDGE,"E62.left")])]});
            var Q7;
            Q7=makeQuery(id+"F34.opExtrude","SWEPT_EDGE",EDGE,{"disambiguationData":[OSD([sQuery(id+"F33.wireOp",EDGE,"E62.bottom"),sQuery(id+"F33.wireOp",EDGE,"E62.left")])]});
            fillet(context, id + "F35", {"entities" : qUnion([Q0, Q1, Q2, Q3, Q4, Q5, Q6, Q7]), "radius" : 5.08 * mm, "tangentPropagation" : true, "allowEdgeOverflow" : false});
        }
        {
            var Q0;
            Q0=makeQuery(id+"F28.opExtrude","SWEPT_EDGE",EDGE,{"disambiguationData":[OSD([sQuery(id+"F27.wireOp",EDGE,"E57.bottom"),sQuery(id+"F27.wireOp",EDGE,"E57.left")])]});
            var Q1;
            Q1=makeQuery(id+"F28.opExtrude","CAP_EDGE",EDGE,{"disambiguationData":[OSD([sQuery(id+"F27.wireOp",EDGE,"E57.left")])],"isStart":false});
            var Q2;
            Q2=makeQuery(id+"F28.opExtrude","CAP_EDGE",EDGE,{"disambiguationData":[OSD([sQuery(id+"F27.wireOp",EDGE,"E57.top")])],"isStart":false});
            var Q3;
            Q3=makeQuery(id+"F28.opExtrude","SWEPT_EDGE",EDGE,{"disambiguationData":[OSD([sQuery(id+"F27.wireOp",EDGE,"E57.top"),sQuery(id+"F27.wireOp",EDGE,"E57.left")])]});
            var Q4;
            Q4=makeQuery(id+"F28.opExtrude","CAP_EDGE",EDGE,{"disambiguationData":[OSD([sQuery(id+"F27.wireOp",EDGE,"E57.bottom")])],"isStart":false});
            var Q5;
            Q5=makeQuery(id+"F32.opExtrude","CAP_EDGE",EDGE,{"disambiguationData":[OSD([sQuery(id+"F29.wireOp",EDGE,"E61.top")])],"isStart":false});
            var Q6;
            Q6=makeQuery(id+"F32.opExtrude","CAP_EDGE",EDGE,{"disambiguationData":[OSD([sQuery(id+"F29.wireOp",EDGE,"E61.left")])],"isStart":false});
            var Q7;
            Q7=makeQuery(id+"F32.opExtrude","SWEPT_EDGE",EDGE,{"disambiguationData":[OSD([sQuery(id+"F29.wireOp",EDGE,"E61.top"),sQuery(id+"F29.wireOp",EDGE,"E61.left")])]});
            var Q8;
            Q8=makeQuery(id+"F32.opExtrude","SWEPT_EDGE",EDGE,{"disambiguationData":[OSD([sQuery(id+"F29.wireOp",EDGE,"E61.bottom"),sQuery(id+"F29.wireOp",EDGE,"E61.left")])]});
            var Q9;
            Q9=makeQuery(id+"F32.opExtrude","CAP_EDGE",EDGE,{"disambiguationData":[OSD([sQuery(id+"F29.wireOp",EDGE,"E61.bottom")])],"isStart":false});
            var Q10;
            Q10=makeQuery(id+"F32.opExtrude","CAP_EDGE",EDGE,{"disambiguationData":[OSD([sQuery(id+"F29.wireOp",EDGE,"E61.right")])],"isStart":false});
            var Q11;
            Q11=makeQuery(id+"F28.opExtrude","CAP_EDGE",EDGE,{"disambiguationData":[OSD([sQuery(id+"F27.wireOp",EDGE,"E57.right")])],"isStart":false});
            var Q12;
            Q12=makeQuery(id+"F28.opExtrude","SWEPT_EDGE",EDGE,{"disambiguationData":[OSD([sQuery(id+"F27.wireOp",EDGE,"E57.bottom"),sQuery(id+"F27.wireOp",EDGE,"E57.right")])]});
            var Q13;
            Q13=makeQuery(id+"F28.opExtrude","SWEPT_EDGE",EDGE,{"disambiguationData":[OSD([sQuery(id+"F27.wireOp",EDGE,"E57.top"),sQuery(id+"F27.wireOp",EDGE,"E57.right")])]});
            var Q14;
            Q14=makeQuery(id+"F32.opExtrude","SWEPT_EDGE",EDGE,{"disambiguationData":[OSD([sQuery(id+"F29.wireOp",EDGE,"E61.bottom"),sQuery(id+"F29.wireOp",EDGE,"E61.right")])]});
            var Q15;
            Q15=makeQuery(id+"F32.opExtrude","SWEPT_EDGE",EDGE,{"disambiguationData":[OSD([sQuery(id+"F29.wireOp",EDGE,"E61.top"),sQuery(id+"F29.wireOp",EDGE,"E61.right")])]});
            fillet(context, id + "F36", {"entities" : qUnion([Q0, Q1, Q2, Q3, Q4, Q5, Q6, Q7, Q8, Q9, Q10, Q11, Q12, Q13, Q14, Q15]), "radius" : 5.08 * mm, "tangentPropagation" : true, "allowEdgeOverflow" : false});
        }
    });
